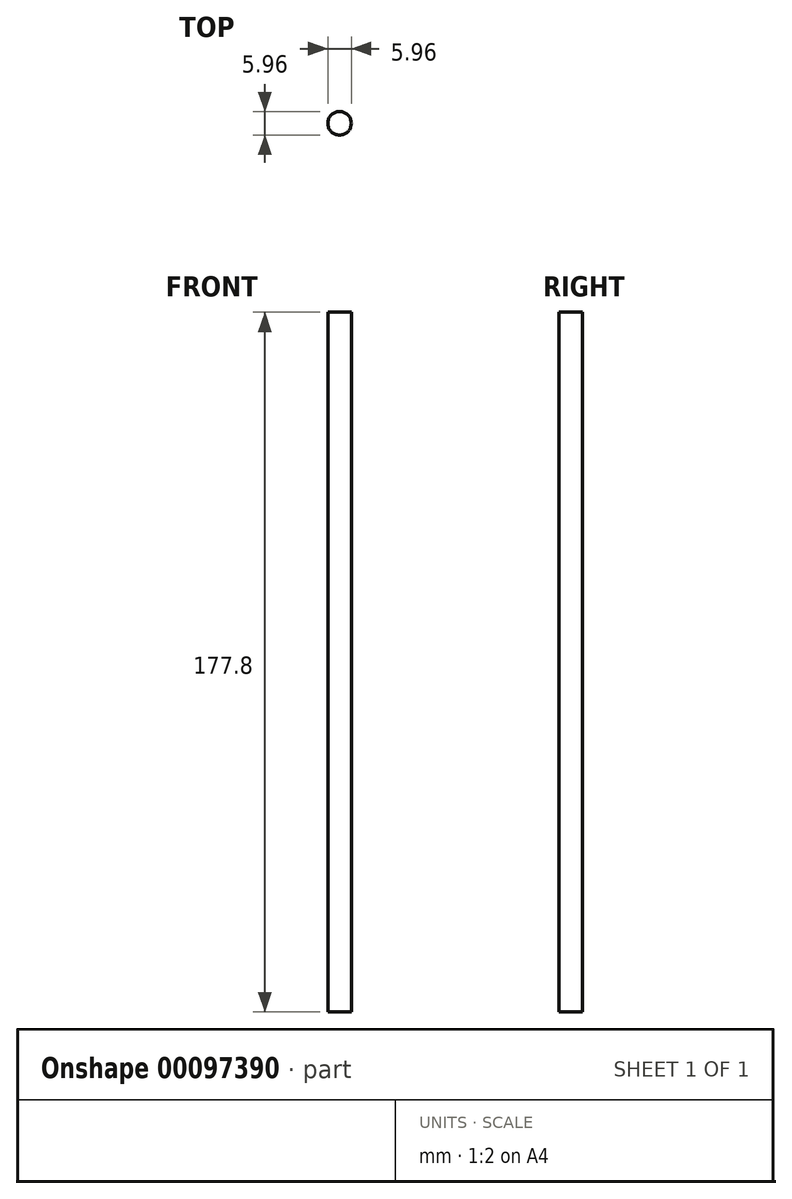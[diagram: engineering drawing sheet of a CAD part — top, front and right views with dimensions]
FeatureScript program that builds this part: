
annotation { "Feature Type Name" : "Feature", "Feature Type Description" : "" }
export const myFeature = defineFeature(function(context is Context, id is Id, definition is map)
    precondition{}
    {
        {
            var Q0;
            Q0=qCreatedBy(makeId("Top.planeOp"),FACE);
            var sketch = newSketch(context, id + "F0", { "sketchPlane" : qUnion([Q0])});
            skCircle(sketch, "E0", {"center": v(0, 0) * mm, "radius": 2.98 * mm});
            skSolve(sketch);
        }
        {
            var Q0;
            Q0=makeQuery(id+"F0.imprint","IMPRINT",FACE,{"disambiguationData":[TD([[makeQuery(id+"F0.imprint","IMPRINT",EDGE,{"derivedFrom":sQuery(id+"F0.wireOp",EDGE,"E0")}),1.0]])]});
            extrude(context, id + "F1", {"entities" : qUnion([Q0]), "oppositeDirection" : true, "depth" : 177.8 * mm});
        }
    });
